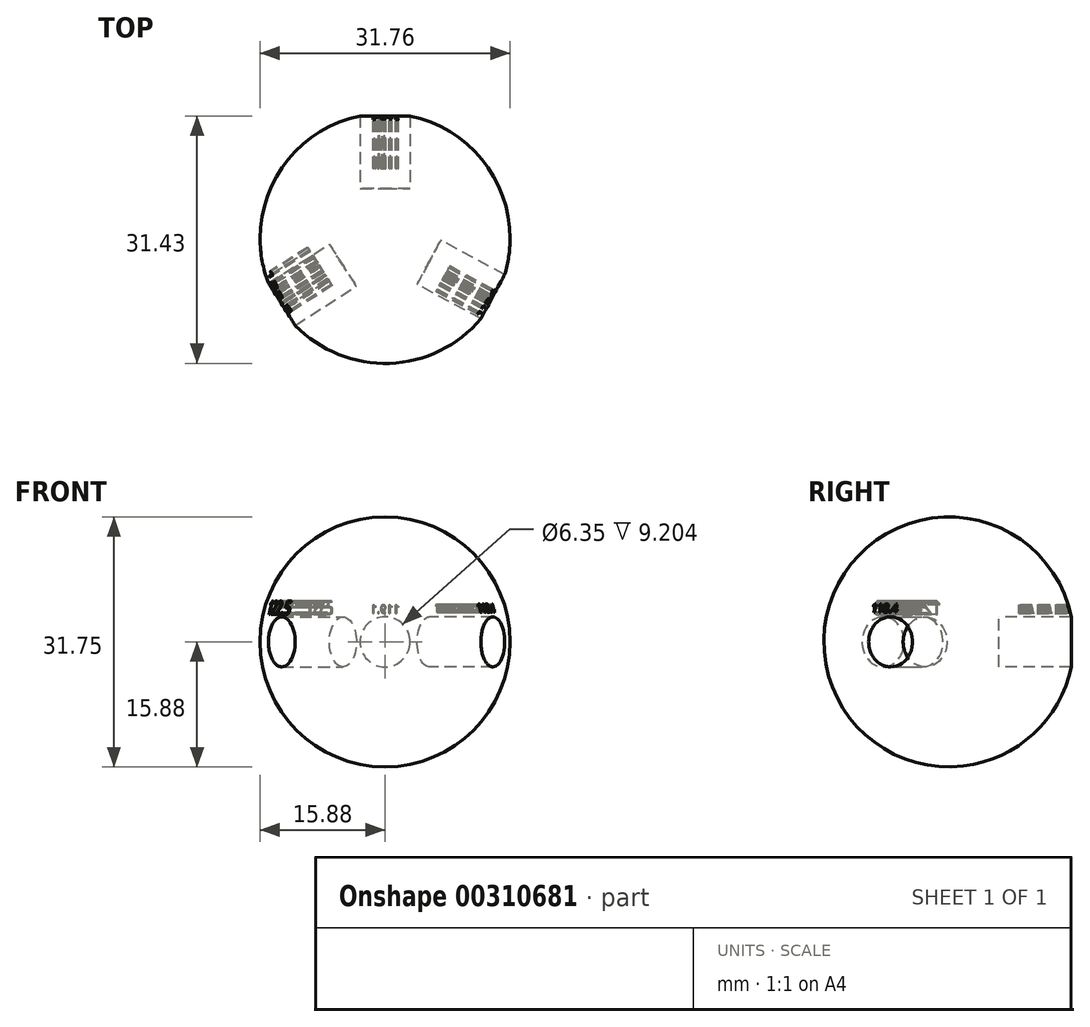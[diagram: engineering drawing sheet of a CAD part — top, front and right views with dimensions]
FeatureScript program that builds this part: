
annotation { "Feature Type Name" : "Feature", "Feature Type Description" : "" }
export const myFeature = defineFeature(function(context is Context, id is Id, definition is map)
    precondition{}
    {
        {
            var Q0;
            Q0=qCreatedBy(makeId("Front.planeOp"),FACE);
            var sketch = newSketch(context, id + "F0", { "sketchPlane" : qUnion([Q0])});
            skArc(sketch, "E0", {"start": v(-15.88, 0) * mm, "mid": v(0, -15.88) * mm, "end": v(15.88, 0) * mm});
            skLineSegment(sketch, "E1", {"start": v(-15.88, 0) * mm, "end": v(15.88, 0) * mm});
            skSolve(sketch);
        }
        {
            var Q0;
            Q0=qCreatedBy(makeId("Right.planeOp"),FACE);
            var sketch = newSketch(context, id + "F1", { "sketchPlane" : qUnion([Q0])});
            skCircle(sketch, "E2", {"center": v(0, 0) * mm, "radius": 15.88 * mm});
            skSolve(sketch);
        }
        {
            var Q0;
            Q0 = qSketchRegion(id + "F0", true);
            var Q1;
            Q1=sQuery(id+"F1.wireOp",EDGE,"E2");
            revolve(context, id + "F2", {"entities" : qUnion([Q0]), "axis" : qUnion([Q1]), "revolveType" : RevolveType.FULL});
        }
        {
            var Q0;
            Q0=qCreatedBy(makeId("Front.planeOp"),FACE);
            cPlane(context, id + "F3", {"entities" : qUnion([Q0]), "cplaneType" : CPlaneType.OFFSET, "offset" : 6.35 * mm, "oppositeDirection" : true, "width" : 152.4 * mm, "height" : 152.4 * mm});
        }
        {
            var Q0;
            Q0=qCreatedBy(id+"F3.planeOp",FACE);
            var sketch = newSketch(context, id + "F4", { "sketchPlane" : qUnion([Q0])});
            skCircle(sketch, "E3", {"center": v(0, 0) * mm, "radius": 3.18 * mm});
            skSolve(sketch);
        }
        {
            var Q0;
            Q0 = qSketchRegion(id + "F4", true);
            extrude(context, id + "F5", {"entities" : qUnion([Q0]), "oppositeDirection" : true, "depth" : 25.4 * mm});
        }
        {
            var Q0;
            Q0=makeQuery(id+"F5.opExtrude","CAP_FACE",FACE,{"disambiguationData":[OSD([sQuery(id+"F4.wireOp",EDGE,"E3")])],"isStart":false});
            cPlane(context, id + "F6", {"entities" : qUnion([Q0]), "cplaneType" : CPlaneType.OFFSET, "offset" : 12.7 * mm, "oppositeDirection" : true, "width" : 152.4 * mm, "height" : 152.4 * mm});
        }
        {
            var Q0;
            Q0=qCreatedBy(id+"F6.planeOp",FACE);
            var sketch = newSketch(context, id + "F7", { "sketchPlane" : qUnion([Q0])});
            skText(sketch, "E4", { "text": "119.1", "fontName": "OpenSans-Regular.ttf"});
            const initialGuessF7  = {"E4": [-0.00185, 0.00364, 1, 0, 0.00105]};
            skSetInitialGuess(sketch, initialGuessF7);
            skSolve(sketch);
        }
        {
            var Q0;
            Q0 = qSketchRegion(id + "F7", true);
            extrude(context, id + "F8", {"entities" : qUnion([Q0]), "operationType" : NewBodyOperationType.REMOVE, "oppositeDirection" : true, "depth" : 10.16 * mm});
        }
        {
            var Q0;
            Q0=qCreatedBy(makeId("Right.planeOp"),FACE);
            var sketch = newSketch(context, id + "F9", { "sketchPlane" : qUnion([Q0])});
            skLineSegment(sketch, "E5", {"start": v(0, 61.57) * mm, "end": v(0, -73.19) * mm, "construction": true});
            skSolve(sketch);
        }
        {
            var Q0;
            Q0=makeQuery(id+"F5.opExtrude","SWEPT_BODY",BODY,{"disambiguationData":[OSD([sQuery(id+"F4.wireOp",EDGE,"E3")])]});
            var Q1;
            Q1=sQuery(id+"F9.wireOp",EDGE,"E5");
            transform(context, id + "F10", {"entities" : qUnion([Q0]), "transformType" : TransformType.ROTATION, "transformAxis" : qUnion([Q1]), "angle" : 118.4 * degree, "makeCopy" : true});
        }
        {
            var Q0;
            Q0=makeQuery(id+"F10.opPattern","COPY",FACE,{"derivedFrom":makeQuery(id+"F5.opExtrude","CAP_FACE",FACE,{"disambiguationData":[OSD([sQuery(id+"F4.wireOp",EDGE,"E3")])],"isStart":false}),"instanceName":"1"});
            cPlane(context, id + "F11", {"entities" : qUnion([Q0]), "cplaneType" : CPlaneType.OFFSET, "offset" : 12.7 * mm, "oppositeDirection" : true, "width" : 152.4 * mm, "height" : 152.4 * mm});
        }
        {
            var Q0;
            Q0=qCreatedBy(id+"F11.planeOp",FACE);
            var sketch = newSketch(context, id + "F12", { "sketchPlane" : qUnion([Q0])});
            skText(sketch, "E6", { "text": "118.4", "fontName": "OpenSans-Regular.ttf"});
            const initialGuessF12  = {"E6": [-0.003, 0.00374, 1, 0, 0.0011]};
            skSetInitialGuess(sketch, initialGuessF12);
            skSolve(sketch);
        }
        {
            var Q0;
            Q0 = qSketchRegion(id + "F12", true);
            extrude(context, id + "F13", {"entities" : qUnion([Q0]), "operationType" : NewBodyOperationType.REMOVE, "oppositeDirection" : true, "depth" : 10.16 * mm});
        }
        {
            var Q0;
            Q0=qCreatedBy(makeId("Right.planeOp"),FACE);
            var sketch = newSketch(context, id + "F14", { "sketchPlane" : qUnion([Q0])});
            skLineSegment(sketch, "E7", {"start": v(0, 54.75) * mm, "end": v(0, -56.41) * mm, "construction": true});
            skSolve(sketch);
        }
        {
            var Q0;
            Q0=makeQuery(id+"F5.opExtrude","SWEPT_BODY",BODY,{"disambiguationData":[OSD([sQuery(id+"F4.wireOp",EDGE,"E3")])]});
            var Q1;
            Q1=sQuery(id+"F14.wireOp",EDGE,"E7");
            transform(context, id + "F15", {"entities" : qUnion([Q0]), "transformType" : TransformType.ROTATION, "transformAxis" : qUnion([Q1]), "angle" : 122.5 * degree, "oppositeDirection" : true, "makeCopy" : true});
        }
        {
            var Q0;
            Q0=makeQuery(id+"F15.opPattern","COPY",FACE,{"derivedFrom":makeQuery(id+"F5.opExtrude","CAP_FACE",FACE,{"disambiguationData":[OSD([sQuery(id+"F4.wireOp",EDGE,"E3")])],"isStart":false}),"instanceName":"1"});
            cPlane(context, id + "F16", {"entities" : qUnion([Q0]), "cplaneType" : CPlaneType.OFFSET, "offset" : 12.7 * mm, "oppositeDirection" : true, "width" : 152.4 * mm, "height" : 152.4 * mm});
        }
        {
            var Q0;
            Q0=qCreatedBy(id+"F16.planeOp",FACE);
            var sketch = newSketch(context, id + "F17", { "sketchPlane" : qUnion([Q0])});
            skText(sketch, "E8", { "text": "122.5\n", "fontName": "OpenSans-Regular.ttf"});
            const initialGuessF17  = {"E8": [-0.00455, 0.00347, 1, 0, 0.00173]};
            skSetInitialGuess(sketch, initialGuessF17);
            skSolve(sketch);
        }
        {
            var Q0;
            Q0 = qSketchRegion(id + "F17", true);
            extrude(context, id + "F18", {"entities" : qUnion([Q0]), "operationType" : NewBodyOperationType.REMOVE, "oppositeDirection" : true, "depth" : 10.16 * mm});
        }
        {
            var Q0;
            Q0=makeQuery(id+"F5.opExtrude","SWEPT_BODY",BODY,{"disambiguationData":[OSD([sQuery(id+"F4.wireOp",EDGE,"E3")])]});
            var Q1;
            Q1=makeQuery(id+"F15.opPattern","COPY",BODY,{"derivedFrom":makeQuery(id+"F5.opExtrude","SWEPT_BODY",BODY,{"disambiguationData":[OSD([sQuery(id+"F4.wireOp",EDGE,"E3")])]}),"instanceName":"1"});
            var Q2;
            Q2=makeQuery(id+"F10.opPattern","COPY",BODY,{"derivedFrom":makeQuery(id+"F5.opExtrude","SWEPT_BODY",BODY,{"disambiguationData":[OSD([sQuery(id+"F4.wireOp",EDGE,"E3")])]}),"instanceName":"1"});
            var Q3;
            Q3=makeQuery(id+"F2.opRevolve","SWEPT_BODY",BODY,{"disambiguationData":[OSD([sQuery(id+"F0.wireOp",EDGE,"E0"),sQuery(id+"F0.wireOp",EDGE,"E1")])]});
            booleanBodies(context, id + "F19", {"operationType" : BooleanOperationType.SUBTRACTION, "tools" : qUnion([Q0, Q1, Q2]), "targets" : qUnion([Q3])});
        }
    });
